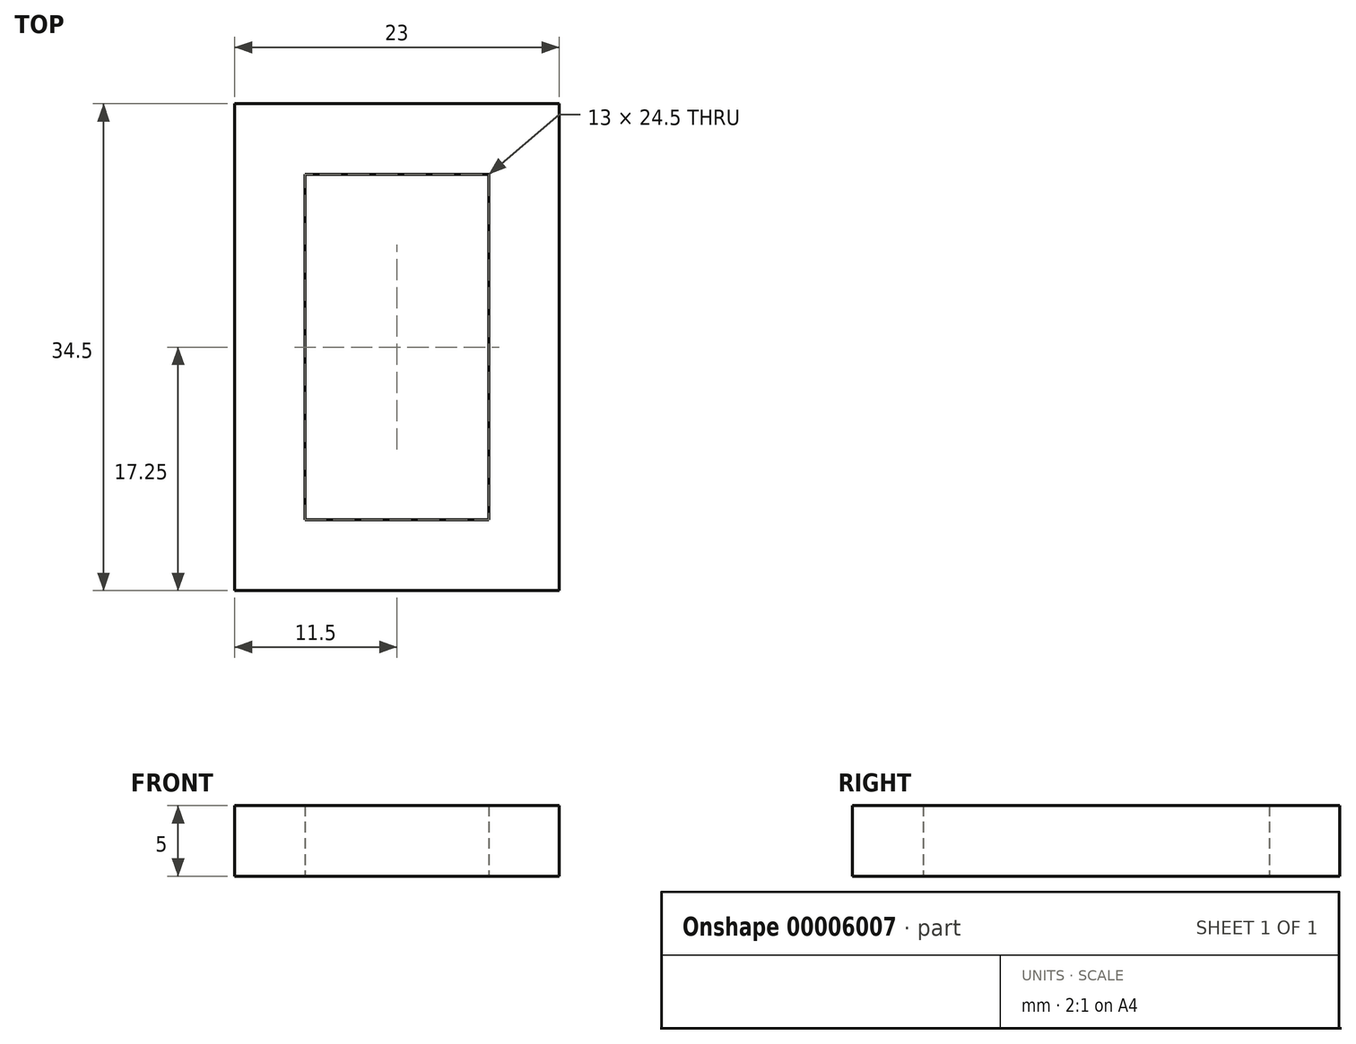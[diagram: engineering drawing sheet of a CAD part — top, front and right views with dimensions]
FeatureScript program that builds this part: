
annotation { "Feature Type Name" : "Feature", "Feature Type Description" : "" }
export const myFeature = defineFeature(function(context is Context, id is Id, definition is map)
    precondition{}
    {
        {
            var Q0;
            Q0=qCreatedBy(makeId("Top.planeOp"),FACE);
            var sketch = newSketch(context, id + "F0", { "sketchPlane" : qUnion([Q0])});
            skLineSegment(sketch, "E0.rect.bottom", {"start": v(6.5, -12.25) * mm, "end": v(-6.5, -12.25) * mm});
            skLineSegment(sketch, "E0.rect.top", {"start": v(6.5, 12.25) * mm, "end": v(-6.5, 12.25) * mm});
            skLineSegment(sketch, "E0.rect.left", {"start": v(6.5, -12.25) * mm, "end": v(6.5, 12.25) * mm});
            skLineSegment(sketch, "E0.rect.right", {"start": v(-6.5, -12.25) * mm, "end": v(-6.5, 12.25) * mm});
            skPoint(sketch, "E0.rect.middle", {"position": v(0, 0) * mm});
            skLineSegment(sketch, "E1.0", {"start": v(11.5, 17.25) * mm, "end": v(-11.5, 17.25) * mm});
            skLineSegment(sketch, "E1.1", {"start": v(11.5, -17.25) * mm, "end": v(11.5, 17.25) * mm});
            skLineSegment(sketch, "E1.2", {"start": v(11.5, -17.25) * mm, "end": v(-11.5, -17.25) * mm});
            skLineSegment(sketch, "E1.3", {"start": v(-11.5, -17.25) * mm, "end": v(-11.5, 17.25) * mm});
            skSolve(sketch);
        }
        {
            var Q0;
            Q0 = qSketchRegion(id + "F0", true);
            extrude(context, id + "F1", {"entities" : qUnion([Q0]), "depth" : 5 * mm});
        }
    });
